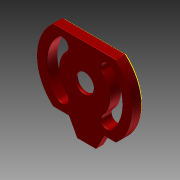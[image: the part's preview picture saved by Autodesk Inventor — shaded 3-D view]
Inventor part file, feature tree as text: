
AUTODESK INVENTOR PART (.ipt)
format: ipt  version: 2013 (Build 170138000, 138)  size: 1,061,888 bytes
history: native  units: in
note: dims shown in document units (in); Inventor stores cm internally (conversion verified against a paired STEP export)
features: sketch x23, extrude x12, sweep x11, plane x9, fillet x7, projected_geometry x6, mirror x3, other x2, shell x1, chamfer x1
ambient origin geometry x8: Origin, YZ Plane, XZ Plane, XY Plane, X Axis, Y Axis, Z Axis, Center Point
bodies: Solid1 (feature_tree)
feature tree (75):
  sketch  "Sketch1"  dims[d0=0.148in d1=0.0in d2=0.118in d3=0.0in]
  extrude  "Extrusion1"  Depth=0.118in TaperAngle=0.0deg
  extrude  "Extrusion2"  Depth=0.118in TaperAngle=0.0deg
  shell  "Shell1"  Thickness=0.108in
  extrude  "Extrusion3"  Depth=0.039in
  sketch  "Sketch4"  dims[d13=0.012in d18=0.008in]
  extrude  "Extrusion4"  Depth=0.008in
  extrude  "Extrusion9"  Depth=0.108in TaperAngle=0.0deg
  fillet  "Fillet1"  Radius=0.098in
  fillet  "Fillet2"  Radius=0.128in
  fillet  "Fillet3"  Radius=0.128in
  fillet  "Fillet7"  Radius=0.02in
  fillet  "Fillet8"  Radius=0.018in
  extrude  "Extrusion6"  Depth=0.0945in
  chamfer  "Chamfer1"  Distance=0.0625in
  extrude  "Extrusion7"  TaperAngle=0.0deg  [1 undecoded]
  extrude  "Extrusion8"  Depth=0.011in
  extrude  "Extrusion10"  TaperAngle=0.0deg  [1 undecoded]
  extrude  "Extrusion11"  Depth=0.0336in
  sketch  "Sketch8"  dims[d39=0.012in]
  sweep  "Sweep1"
  sweep  "Sweep2"
  sketch  "Sketch10"  dims[d41=0.012in]
  plane  "Work Plane1"
  sweep  "Sweep3"
  sweep  "Sweep4"
  sweep  "Sweep5"
  plane  "Work Plane2"
  sweep  "Sweep7"
  plane  "Work Plane4"
  sketch  "Sketch15"  dims[d46=0.0in]
  plane  "Work Plane5"
  extrude  "Extrusion12"  Depth=0.016in
  sweep  "Sweep9"
  sweep  "Sweep10"
  plane  "Work Plane6"
  sketch  "Sketch19"  dims[d50=0.0in]
  other  "Work Axis2"
  plane  "Work Plane7"
  mirror  "Mirror2"
  sketch  "Sketch20"  dims[d51=90.0deg d53=0.0625in d54=0.0in]
  sweep  "Sweep12"
  mirror  "Mirror3"
  sketch  "Sketch21"  dims[d55=0.0in d56=0.0in]
  sweep  "Sweep13"
  plane  "Work Plane8"
  sweep  "Sweep14"
  plane  "Work Plane9"
  mirror  "Mirror4"
  extrude  "Extrusion13"  [1 undecoded]
  fillet  "Fillet10"  [1 undecoded]
  fillet  "Fillet11"  [1 undecoded]
  sketch  "Sketch2"  dims[d4=0.039in d5=0.118in d6=0.0in d7=0.108in d8=0.0in]
  sketch  "Sketch3"  dims[d11=0.008in d12=0.039in]
  sketch  "Sketch5"  dims[d19=0.016in d20=0.108in d21=0.0in]
  sketch  "Sketch6"  dims[d23=0.012in d24=0.125in d25=45.0deg d26=0.098in d27=0.0in d28=0.128in d29=0.0in d30=0.128in d31=0.0in d32=0.02in d33=0.0in d34=0.018in d35=0.0in]
  sketch  "Sketch7"  dims[d37=0.189in d38=0.0945in]
  sketch  "Sketch9"  dims[d40=0.012in]
  sketch  "Sketch11"  dims[d42=0.0in]
  projected_geometry  "Projected Loop1"
  sketch  "Sketch12"  dims[d43=0.0in]
  sketch  "Sketch13"  dims[d44=0.0in]
  sketch  "Sketch14"  dims[d45=0.0in]
  projected_geometry  "Projected Loop2"
  other  "Work Axis1"
  plane  "Work Plane3"
  sketch  "Sketch17"  dims[d48=0.1443in]
  sketch  "Sketch18"  dims[d49=0.0721in]
  sketch  "Sketch22"  dims[d57=90.0deg d61=0.011in]
  sketch  "Sketch23"  dims[d62=0.013in d64=0.0in]
  projected_geometry  "Projected Loop4"
  projected_geometry  "Projected Loop5"
  sketch  "Sketch24"  dims[d65=0.0in d66=0.0336in d67=0.0in d68=90.0deg d69=0.0in d70=90.0deg d71=0.0625in d72=0.0in d73=0.02in d74=0.016in d75=0.016in]
  projected_geometry  "Projected Loop6"
  projected_geometry  "Project Cut Edges1"
note: 5 required parameter values undecoded (feature->parameter linkage not recoverable at this tier; creation-order binding heuristic only, values carry confidence <= 0.55)
